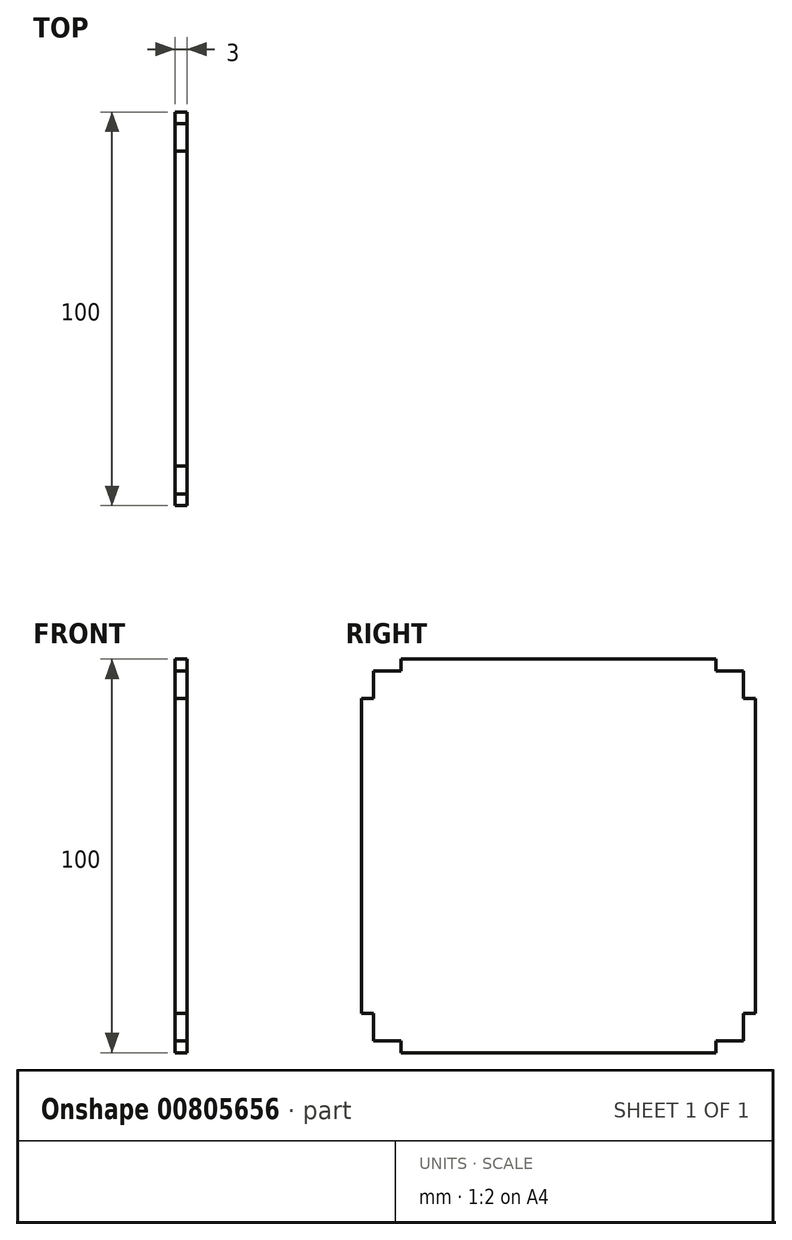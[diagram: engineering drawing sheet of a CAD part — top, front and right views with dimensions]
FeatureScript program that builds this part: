
annotation { "Feature Type Name" : "Feature", "Feature Type Description" : "" }
export const myFeature = defineFeature(function(context is Context, id is Id, definition is map)
    precondition{}
    {
        {
            var Q0;
            Q0=qCreatedBy(makeId("Right.planeOp"),FACE);
            var sketch = newSketch(context, id + "F0", { "sketchPlane" : qUnion([Q0])});
            skLineSegment(sketch, "E0.bottom", {"start": v(10, 0) * mm, "end": v(90, 0) * mm});
            skLineSegment(sketch, "E0.top", {"start": v(10, 100) * mm, "end": v(90, 100) * mm});
            skLineSegment(sketch, "E0.left", {"start": v(0, 10) * mm, "end": v(0, 90) * mm});
            skLineSegment(sketch, "E0.right", {"start": v(100, 10) * mm, "end": v(100, 90) * mm});
            skLineSegment(sketch, "E1", {"start": v(3, 97) * mm, "end": v(10, 97) * mm});
            skLineSegment(sketch, "E2", {"start": v(10, 97) * mm, "end": v(10, 100) * mm});
            skLineSegment(sketch, "E3", {"start": v(3, 97) * mm, "end": v(3, 90) * mm});
            skLineSegment(sketch, "E4", {"start": v(3, 90) * mm, "end": v(0, 90) * mm});
            skLineSegment(sketch, "E5", {"start": v(50, 100) * mm, "end": v(50, 0) * mm, "construction": true});
            skLineSegment(sketch, "E6", {"start": v(0, 50) * mm, "end": v(100, 50) * mm, "construction": true});
            skPoint(sketch, "E7.orphan", {"position": v(0, 100) * mm});
            skLineSegment(sketch, "E8.MirrorCS", {"start": v(90, 97) * mm, "end": v(90, 100) * mm});
            skLineSegment(sketch, "E9.MirrorCS", {"start": v(97, 97) * mm, "end": v(90, 97) * mm});
            skLineSegment(sketch, "E10.MirrorCS", {"start": v(97, 97) * mm, "end": v(97, 90) * mm});
            skLineSegment(sketch, "E11.MirrorCS", {"start": v(97, 90) * mm, "end": v(100, 90) * mm});
            skPoint(sketch, "E12.orphan", {"position": v(100, 100) * mm});
            skLineSegment(sketch, "E13.MirrorCS", {"start": v(3, 10) * mm, "end": v(0, 10) * mm});
            skLineSegment(sketch, "E14.MirrorCS", {"start": v(3, 3) * mm, "end": v(3, 10) * mm});
            skLineSegment(sketch, "E15.MirrorCS", {"start": v(3, 3) * mm, "end": v(10, 3) * mm});
            skLineSegment(sketch, "E16.MirrorCS", {"start": v(10, 3) * mm, "end": v(10, 0) * mm});
            skLineSegment(sketch, "E17.MirrorCS", {"start": v(90, 3) * mm, "end": v(90, 0) * mm});
            skLineSegment(sketch, "E18.MirrorCS", {"start": v(97, 3) * mm, "end": v(90, 3) * mm});
            skLineSegment(sketch, "E19.MirrorCS", {"start": v(97, 3) * mm, "end": v(97, 10) * mm});
            skLineSegment(sketch, "E20.MirrorCS", {"start": v(97, 10) * mm, "end": v(100, 10) * mm});
            skPoint(sketch, "E21.orphan", {"position": v(100, 0) * mm});
            skPoint(sketch, "E22.orphan", {"position": v(0, 0) * mm});
            skSolve(sketch);
        }
        {
            var Q0;
            Q0 = qSketchRegion(id + "F0", true);
            extrude(context, id + "F1", {"entities" : qUnion([Q0]), "depth" : 3 * mm, "offsetDistance" : 25 * mm});
        }
    });
